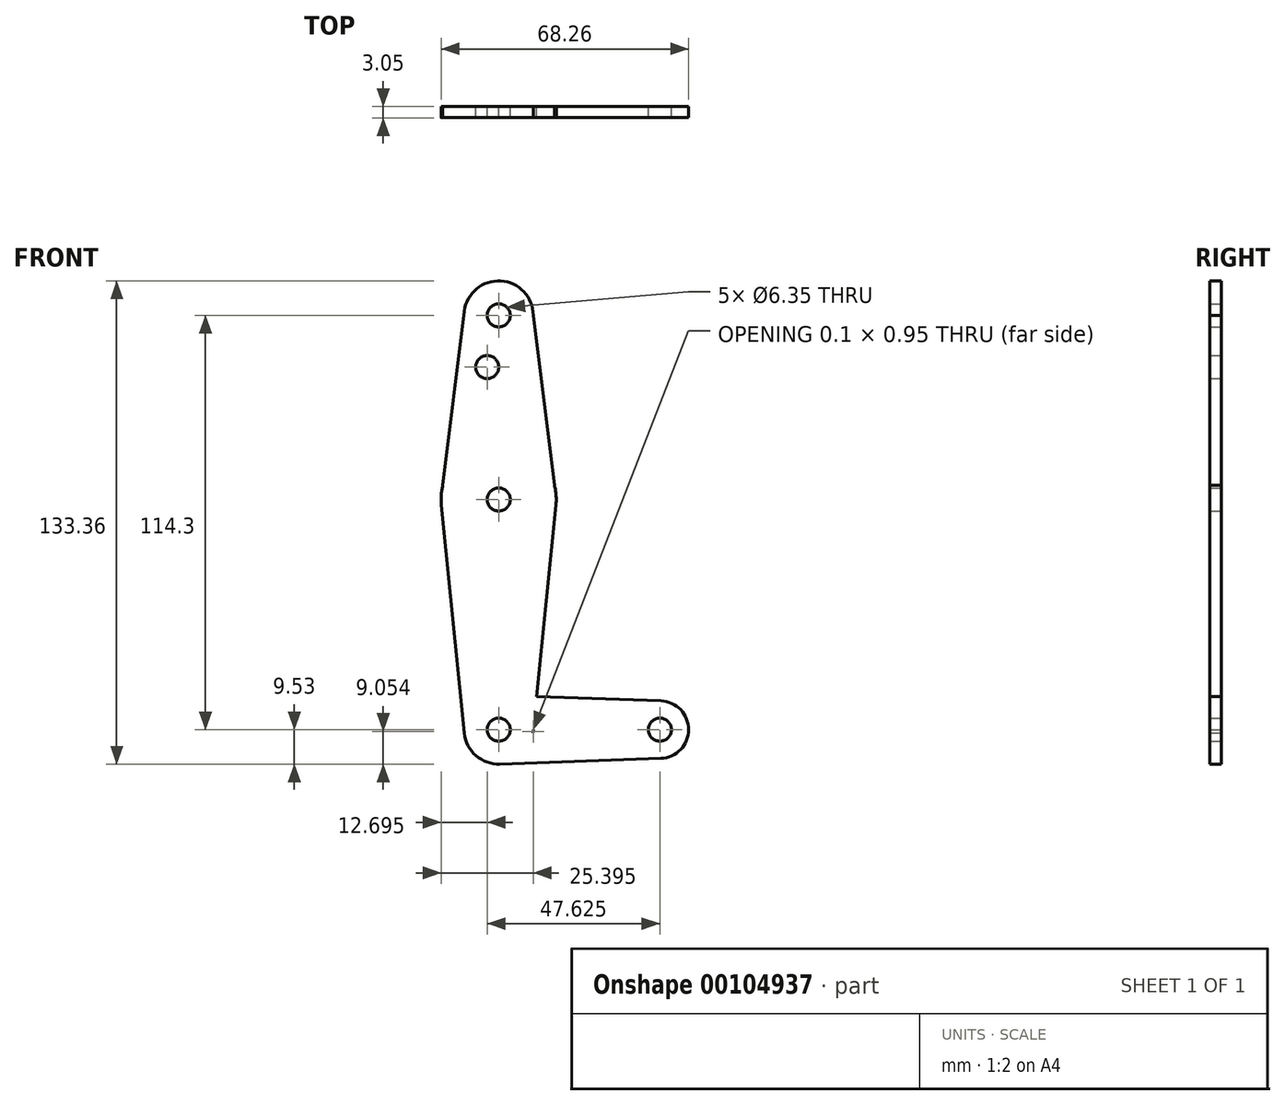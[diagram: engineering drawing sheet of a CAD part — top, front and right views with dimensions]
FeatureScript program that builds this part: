
annotation { "Feature Type Name" : "Feature", "Feature Type Description" : "" }
export const myFeature = defineFeature(function(context is Context, id is Id, definition is map)
    precondition{}
    {
        {
            var Q0;
            Q0=qCreatedBy(makeId("Front.planeOp"),FACE);
            var sketch = newSketch(context, id + "F0", { "sketchPlane" : qUnion([Q0])});
            skLineSegment(sketch, "E0", {"start": v(0, 114.3) * mm, "end": v(0, 0) * mm});
            skLineSegment(sketch, "E1", {"start": v(0, 0) * mm, "end": v(44.45, 0) * mm});
            skCircle(sketch, "E2", {"center": v(0, 114.3) * mm, "radius": 9.53 * mm});
            skCircle(sketch, "E3", {"center": v(0, 63.5) * mm, "radius": 15.88 * mm});
            skCircle(sketch, "E4", {"center": v(0, 0) * mm, "radius": 9.53 * mm});
            skCircle(sketch, "E5", {"center": v(44.45, 0) * mm, "radius": 7.94 * mm});
            skLineSegment(sketch, "E6", {"start": v(-9.45, 115.47) * mm, "end": v(-15.87, 63.5) * mm});
            skArc(sketch, "E7", {"start": v(-9.53, 0) * mm, "mid": v(-6.74, -6.74) * mm, "end": v(0, -9.53) * mm});
            skArc(sketch, "E8", {"start": v(44.45, -7.94) * mm, "mid": v(50.06, -5.61) * mm, "end": v(52.39, 0) * mm});
            skArc(sketch, "E9", {"start": v(52.39, 0) * mm, "mid": v(50.06, 5.61) * mm, "end": v(44.45, 7.94) * mm});
            skArc(sketch, "E10", {"start": v(0, 123.83) * mm, "mid": v(-6.3, 121.44) * mm, "end": v(-9.45, 115.47) * mm});
            skArc(sketch, "E11", {"start": v(9.53, 114.3) * mm, "mid": v(6.74, 121.04) * mm, "end": v(0, 123.83) * mm});
            skLineSegment(sketch, "E12", {"start": v(9.53, 114.3) * mm, "end": v(15.88, 63.5) * mm});
            skLineSegment(sketch, "E13", {"start": v(-15.8, 61.91) * mm, "end": v(-9.48, -0.95) * mm});
            skLineSegment(sketch, "E14", {"start": v(0.34, 9.52) * mm, "end": v(44.73, 7.93) * mm});
            skLineSegment(sketch, "E15", {"start": v(0.34, -9.52) * mm, "end": v(44.73, -7.93) * mm});
            skLineSegment(sketch, "E16", {"start": v(15.8, 61.91) * mm, "end": v(9.48, -0.95) * mm});
            skCircle(sketch, "E17", {"center": v(0, 114.3) * mm, "radius": 3.18 * mm});
            skCircle(sketch, "E18", {"center": v(0, 63.5) * mm, "radius": 3.18 * mm});
            skCircle(sketch, "E19", {"center": v(0, 0) * mm, "radius": 3.18 * mm});
            skCircle(sketch, "E20", {"center": v(44.45, 0) * mm, "radius": 3.18 * mm});
            skCircle(sketch, "E21", {"center": v(-3.17, 100.03) * mm, "radius": 3.18 * mm});
            skSolve(sketch);
        }
        {
            var Q0;
            Q0 = qSketchRegion(id + "F0", true);
            var Q1;
            {var subQ0=sQuery(id+"F0.wireOp",EDGE,"E4");var subQ6=sQuery(id+"F0.wireOp",EDGE,"E0");var subQ7=makeQuery(id+"F0.imprint","INTERSECT",VERTEX,{"derivedFrom":[subQ6,subQ0]});Q1=makeQuery(id+"F0.imprint","IMPRINT",FACE,{"disambiguationData":[TD([[makeQuery(id+"F0.imprint","IMPRINT",EDGE,{"disambiguationData":[TD([[subQ7,-1.0]])],"derivedFrom":subQ6}),1.0]])]});}
            extrude(context, id + "F1", {"entities" : qUnion([Q0, Q1]), "depth" : 3.05 * mm});
        }
    });
